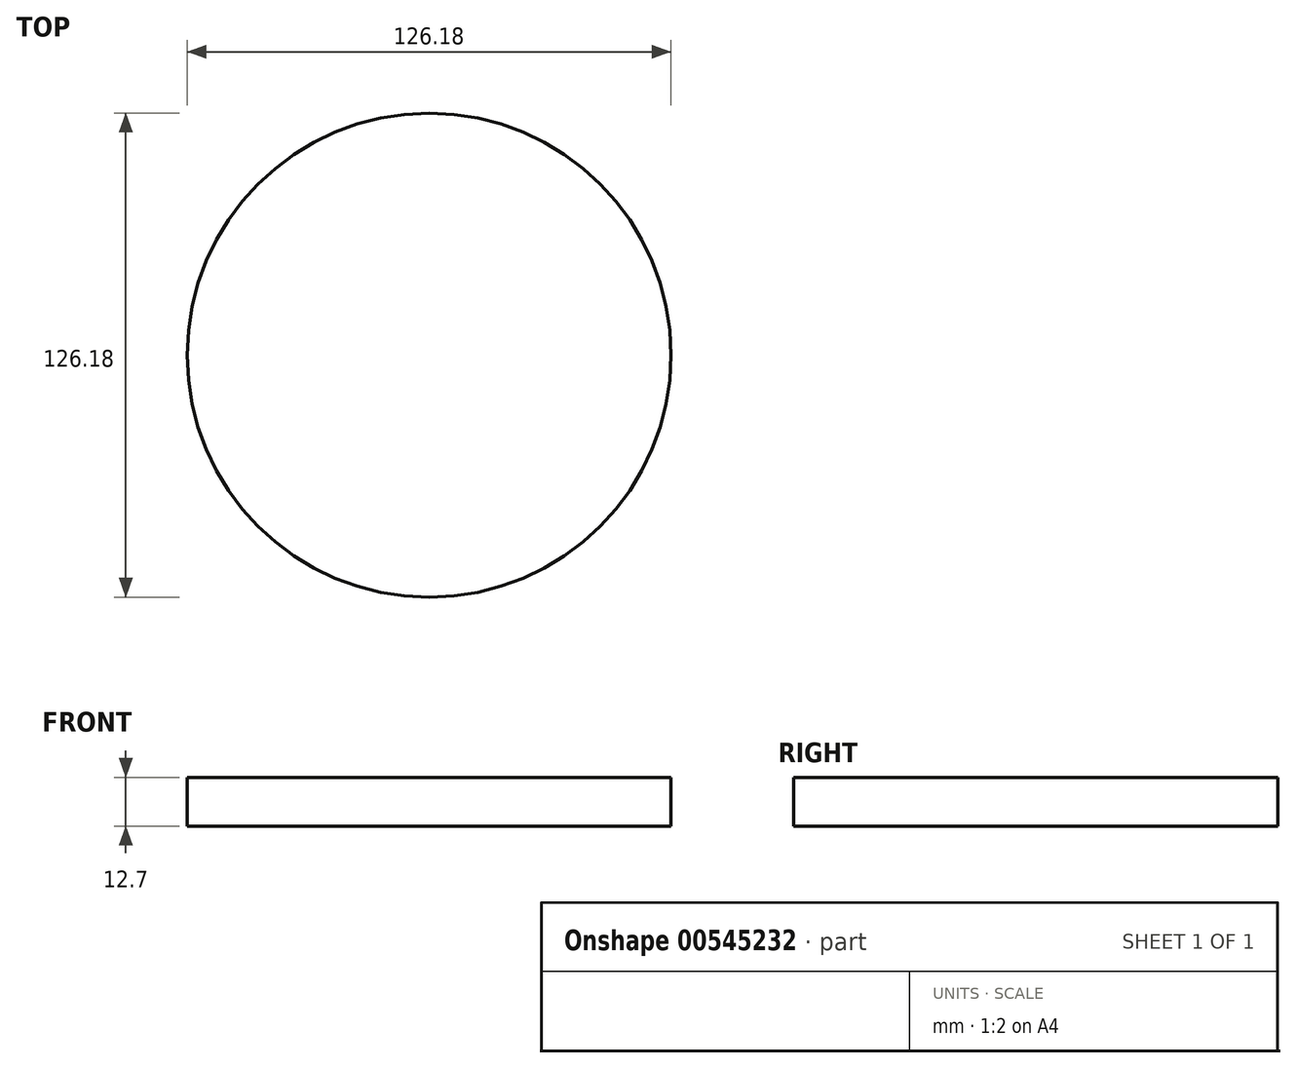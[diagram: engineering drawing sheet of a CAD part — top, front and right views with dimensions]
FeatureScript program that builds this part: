
annotation { "Feature Type Name" : "Feature", "Feature Type Description" : "" }
export const myFeature = defineFeature(function(context is Context, id is Id, definition is map)
    precondition{}
    {
        {
            var Q0;
            Q0=qCreatedBy(makeId("Top.planeOp"),FACE);
            var sketch = newSketch(context, id + "F0", { "sketchPlane" : qUnion([Q0])});
            skCircle(sketch, "E0", {"center": v(0, 0) * mm, "radius": 63.09 * mm});
            skSolve(sketch);
        }
        {
            var Q0;
            Q0 = qSketchRegion(id + "F0", true);
            extrude(context, id + "F1", {"entities" : qUnion([Q0]), "depth" : 12.7 * mm, "offsetDistance" : 25.4 * mm});
        }
    });
